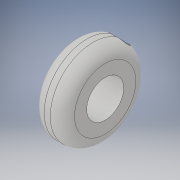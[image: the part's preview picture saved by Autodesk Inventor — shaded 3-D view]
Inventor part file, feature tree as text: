
AUTODESK INVENTOR PART (.ipt)
format: ipt  version: 2019 (Build 230136000, 136)  size: 171,520 bytes
history: native  units: in
note: dims shown in document units (in); Inventor stores cm internally (conversion verified against a paired STEP export)
features: sketch x3, extrude x2, plane x1, thread x1, fillet x1
ambient origin geometry x8: Origin, YZ Plane, XZ Plane, XY Plane, X Axis, Y Axis, Z Axis, Center Point
bodies: Solid1 (feature_tree)
feature tree (8):
  extrude  "Extrusion1"  Depth=0.1575in
  sketch  "Sketch2"  dims[d2=0.1969in d3=0.0in d4=45.0deg d5=0.1969in d6=180.0deg]
  plane  "Work Plane1"
  extrude  "Extrusion2"  TaperAngle=45.0deg  [1 undecoded]
  thread  "Thread1"  [1 undecoded]
  fillet  "Fillet1"  [1 undecoded]
  sketch  "Sketch1"  dims[d0=0.2402in d1=0.1575in]
  sketch  "Sketch3"  dims[d7=0.1181in d8=0.1969in d9=0.0in d10=0.3937in d11=0.0in d12=0.0787in]
note: 3 required parameter values undecoded (feature->parameter linkage not recoverable at this tier; creation-order binding heuristic only, values carry confidence <= 0.55)
